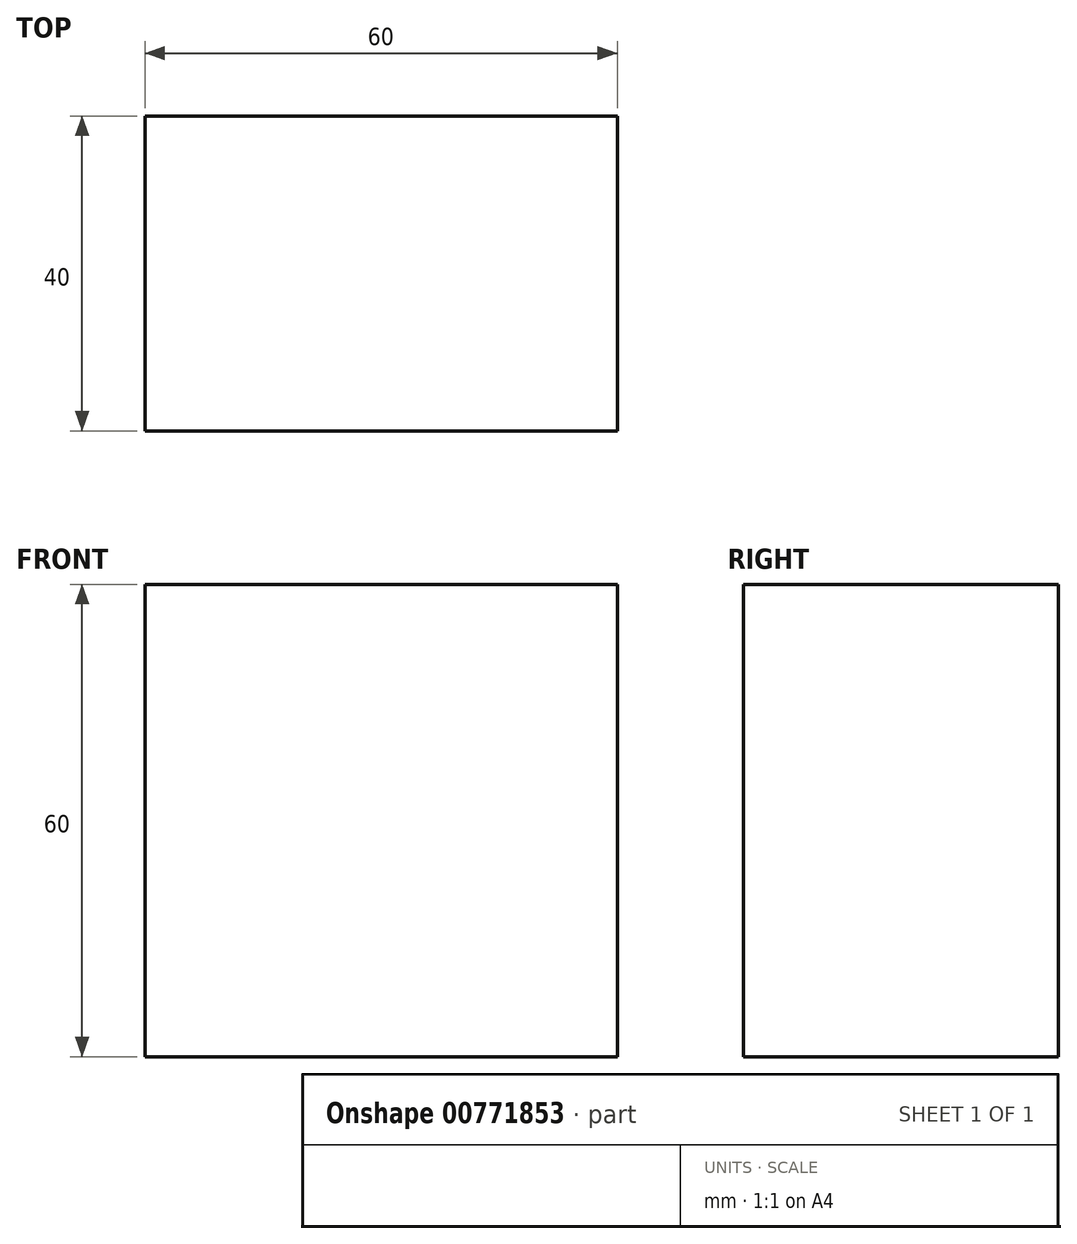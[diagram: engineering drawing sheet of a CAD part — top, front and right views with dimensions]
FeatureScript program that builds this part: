
annotation { "Feature Type Name" : "Feature", "Feature Type Description" : "" }
export const myFeature = defineFeature(function(context is Context, id is Id, definition is map)
    precondition{}
    {
        {
            var Q0;
            Q0=qCreatedBy(makeId("Front.planeOp"),FACE);
            var sketch = newSketch(context, id + "F0", { "sketchPlane" : qUnion([Q0])});
            skLineSegment(sketch, "E0", {"start": v(0, 0) * mm, "end": v(0, 60) * mm});
            skLineSegment(sketch, "E1", {"start": v(0, 60) * mm, "end": v(60, 60) * mm});
            skLineSegment(sketch, "E2", {"start": v(60, 60) * mm, "end": v(60, 0) * mm});
            skLineSegment(sketch, "E3", {"start": v(60, 0) * mm, "end": v(0, 0) * mm});
            skSolve(sketch);
        }
        {
            var Q0;
            Q0 = qSketchRegion(id + "F0", true);
            extrude(context, id + "F1", {"entities" : qUnion([Q0]), "depth" : 40 * mm, "offsetDistance" : 25 * mm});
        }
    });
